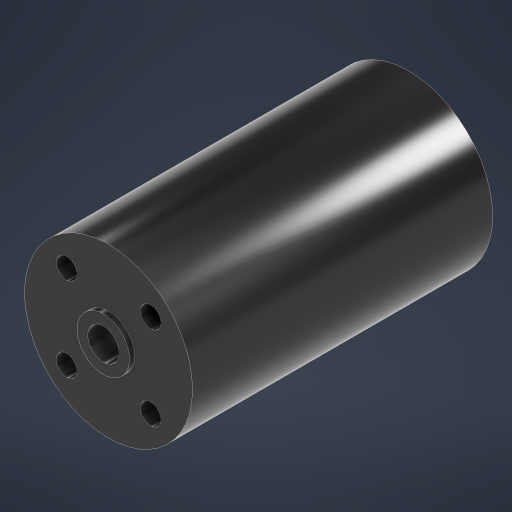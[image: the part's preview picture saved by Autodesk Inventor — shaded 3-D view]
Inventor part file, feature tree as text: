
AUTODESK INVENTOR PART (.ipt)
format: ipt  version: 2023.2 (Build 272271000, 271)  size: 252,416 bytes
history: native  units: mm
features: extrude x4, sketch x1, mirror x1
ambient origin geometry x8: Origin, YZ Plane, XZ Plane, XY Plane, X Axis, Y Axis, Z Axis, Center Point
bodies: Volumenkörper1 (feature_tree)
feature tree (6):
  sketch  "Skizze1"  dims[d0=32.0mm d1=4.0mm d2=8.0mm d3=8.0mm d4=20.0mm d6=16.0mm d7=20.0mm d9=16.0mm d12=57.2mm d13=0.0mm d14=10.0mm d15=0.0mm d16=10.0mm d17=1.0mm d18=0.0mm d19=6.0mm d20=0.0mm d21=0.0mm]
  extrude  "Extrusion1"  Depth=1.0mm
  extrude  "Extrusion2"  Depth=1.0mm
  extrude  "Extrusion3"  Depth=1.0mm
  extrude  "Extrusion4"  Depth=16.0mm
  mirror  "Spiegeln1"
